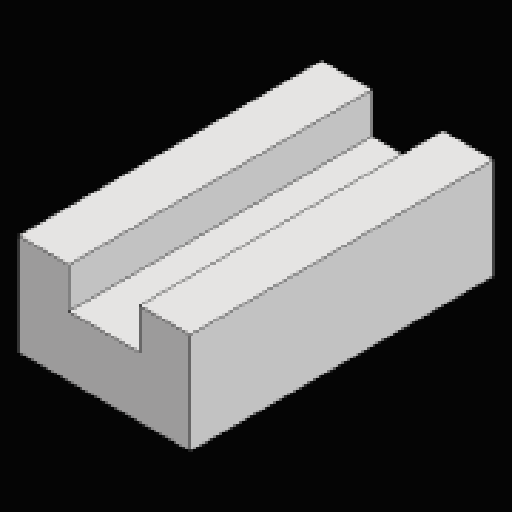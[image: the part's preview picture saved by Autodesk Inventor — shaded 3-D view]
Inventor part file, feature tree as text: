
AUTODESK INVENTOR PART (.ipt)
format: ipt  version: 2023.2 (Build 272271030, 271C)  size: 92,672 bytes
history: native  units: mm
features: extrude x1, sketch x1
ambient origin geometry x8: Origin, YZ Plane, XZ Plane, XY Plane, X Axis, Y Axis, Z Axis, Center Point
bodies: Solid1 (feature_tree)
feature tree (2):
  extrude  "Extrusion1"  Depth=4.0mm
  sketch  "Sketch1"  dims[d0=17.0mm d2=4.0mm d3=7.0mm d4=5.0mm d5=6.0mm d6=30.0mm d7=0.0mm]
